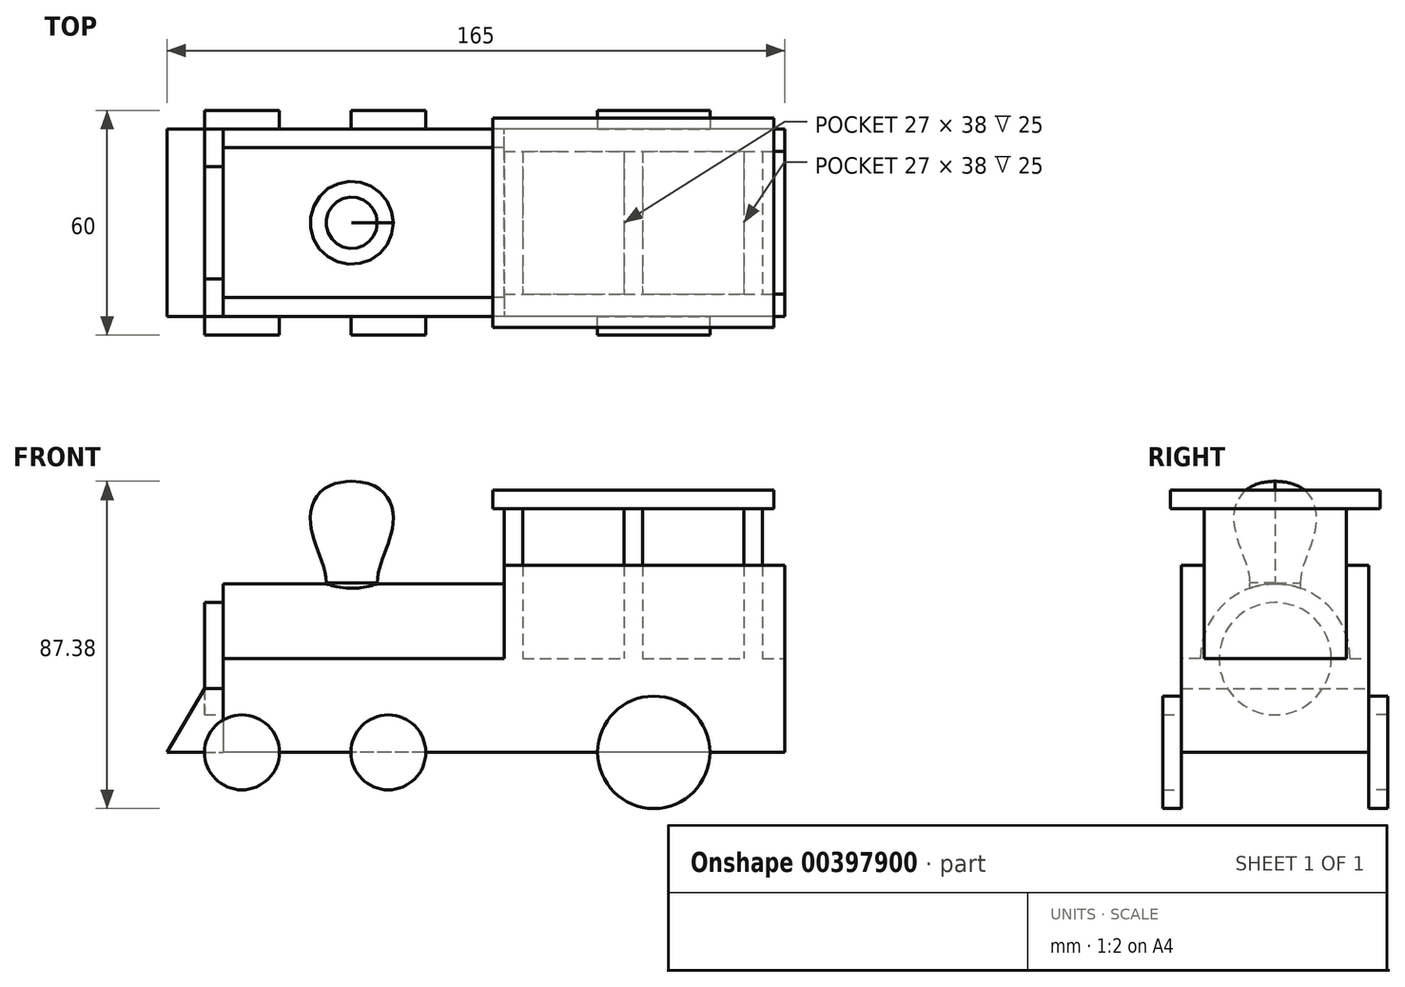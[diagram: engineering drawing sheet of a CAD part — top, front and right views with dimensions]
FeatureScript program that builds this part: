
annotation { "Feature Type Name" : "Feature", "Feature Type Description" : "" }
export const myFeature = defineFeature(function(context is Context, id is Id, definition is map)
    precondition{}
    {
        {
            var Q0;
            Q0=qCreatedBy(makeId("Top.planeOp"),FACE);
            var sketch = newSketch(context, id + "F0", { "sketchPlane" : qUnion([Q0])});
            skLineSegment(sketch, "E0.bottom", {"start": v(75, 25) * mm, "end": v(-75, 25) * mm});
            skLineSegment(sketch, "E0.top", {"start": v(75, -25) * mm, "end": v(-75, -25) * mm});
            skLineSegment(sketch, "E0.left", {"start": v(75, 25) * mm, "end": v(75, -25) * mm});
            skLineSegment(sketch, "E0.right", {"start": v(-75, 25) * mm, "end": v(-75, -25) * mm});
            skPoint(sketch, "E0.middle", {"position": v(0, 0) * mm});
            skSolve(sketch);
        }
        {
            var Q0;
            Q0=makeQuery(id+"F0.imprint","IMPRINT",FACE,{"disambiguationData":[TD([[makeQuery(id+"F0.imprint","IMPRINT",EDGE,{"derivedFrom":sQuery(id+"F0.wireOp",EDGE,"E0.bottom")}),1.0]])]});
            extrude(context, id + "F1", {"entities" : qUnion([Q0]), "depth" : 25 * mm});
        }
        {
            var Q0;
            Q0=makeQuery(id+"F1.opExtrude","SWEPT_FACE",FACE,{"disambiguationData":[OSD([sQuery(id+"F0.wireOp",EDGE,"E0.right")])]});
            var sketch = newSketch(context, id + "F2", { "sketchPlane" : qUnion([Q0])});
            skCircle(sketch, "E1", {"center": v(0, 25) * mm, "radius": 20 * mm});
            skSolve(sketch);
        }
        {
            var Q0;
            Q0=makeQuery(id+"F1.opExtrude","CAP_FACE",FACE,{"disambiguationData":[OSD([sQuery(id+"F0.wireOp",EDGE,"E0.bottom"),sQuery(id+"F0.wireOp",EDGE,"E0.top"),sQuery(id+"F0.wireOp",EDGE,"E0.left"),sQuery(id+"F0.wireOp",EDGE,"E0.right")])],"isStart":false});
            var sketch = newSketch(context, id + "F3", { "sketchPlane" : qUnion([Q0])});
            skLineSegment(sketch, "E2", {"start": v(0, 25) * mm, "end": v(0, -25) * mm, "construction": true});
            skSolve(sketch);
        }
        {
            var Q0;
            {var subQ0=sQuery(id+"F2.wireOp",EDGE,"E1");var subQ1=makeQuery(id+"F1.opExtrude","CAP_EDGE",EDGE,{"disambiguationData":[OSD([sQuery(id+"F0.wireOp",EDGE,"E0.right")])],"isStart":false});var subQ2=makeQuery(id+"F2.imprint","INTERSECT",VERTEX,{"disambiguationData":[OD(0.0)],"derivedFrom":[subQ1,subQ0]});Q0=makeQuery(id+"F2.imprint","IMPRINT",FACE,{"disambiguationData":[TD([[makeQuery(id+"F2.imprint","IMPRINT",EDGE,{"disambiguationData":[TD([[subQ2,1.0]])],"derivedFrom":subQ0}),1.0]])]});}
            extrude(context, id + "F4", {"entities" : qUnion([Q0]), "operationType" : NewBodyOperationType.ADD, "oppositeDirection" : true, "depth" : 75 * mm});
        }
        {
            var Q0;
            Q0=makeQuery(id+"F3.imprint","IMPRINT",FACE,{"disambiguationData":[TD([[makeQuery(id+"F3.imprint","IMPRINT",EDGE,{"derivedFrom":makeQuery(id+"F1.opExtrude","CAP_EDGE",EDGE,{"disambiguationData":[OSD([sQuery(id+"F0.wireOp",EDGE,"E0.bottom")])],"isStart":false})}),1.0]])]});
            var sketch = newSketch(context, id + "F5", { "sketchPlane" : qUnion([Q0])});
            skLineSegment(sketch, "E3.bottom", {"start": v(5, 19) * mm, "end": v(0, 19) * mm});
            skLineSegment(sketch, "E3.top", {"start": v(5, -19) * mm, "end": v(0, -19) * mm});
            skLineSegment(sketch, "E3.left", {"start": v(5, 19) * mm, "end": v(5, -19) * mm});
            skLineSegment(sketch, "E3.right", {"start": v(0, 19) * mm, "end": v(0, -19) * mm});
            skPoint(sketch, "E3.middle", {"position": v(2.5, 0) * mm});
            skLineSegment(sketch, "E4.1.0.0", {"start": v(32, 19) * mm, "end": v(32, -19) * mm});
            skLineSegment(sketch, "E4.1.0.1", {"start": v(37, -19) * mm, "end": v(32, -19) * mm});
            skLineSegment(sketch, "E4.1.0.2", {"start": v(37, 19) * mm, "end": v(37, -19) * mm});
            skLineSegment(sketch, "E4.1.0.3", {"start": v(37, 19) * mm, "end": v(32, 19) * mm});
            skPoint(sketch, "E4.1.0.4", {"position": v(34.5, 0) * mm});
            skLineSegment(sketch, "E4.2.0.0", {"start": v(64, 19) * mm, "end": v(64, -19) * mm});
            skLineSegment(sketch, "E4.2.0.1", {"start": v(69, -19) * mm, "end": v(64, -19) * mm});
            skLineSegment(sketch, "E4.2.0.2", {"start": v(69, 19) * mm, "end": v(69, -19) * mm});
            skLineSegment(sketch, "E4.2.0.3", {"start": v(69, 19) * mm, "end": v(64, 19) * mm});
            skPoint(sketch, "E4.2.0.4", {"position": v(66.5, 0) * mm});
            skLineSegment(sketch, "E4.direction1", {"start": v(0, -19) * mm, "end": v(32, -19) * mm, "construction": true});
            skSolve(sketch);
        }
        {
            var Q0;
            Q0 = qSketchRegion(id + "F5", true);
            extrude(context, id + "F6", {"entities" : qUnion([Q0]), "operationType" : NewBodyOperationType.ADD, "depth" : 40 * mm});
        }
        {
            var Q0;
            Q0=makeQuery(id+"F3.imprint","IMPRINT",FACE,{"disambiguationData":[TD([[makeQuery(id+"F3.imprint","IMPRINT",EDGE,{"derivedFrom":makeQuery(id+"F1.opExtrude","CAP_EDGE",EDGE,{"disambiguationData":[OSD([sQuery(id+"F0.wireOp",EDGE,"E0.bottom")])],"isStart":false})}),1.0]])]});
            var sketch = newSketch(context, id + "F7", { "sketchPlane" : qUnion([Q0])});
            skLineSegment(sketch, "E5.bottom", {"start": v(0, 19) * mm, "end": v(75, 19) * mm});
            skLineSegment(sketch, "E5.top", {"start": v(0, 25) * mm, "end": v(75, 25) * mm});
            skLineSegment(sketch, "E5.left", {"start": v(0, 19) * mm, "end": v(0, 25) * mm});
            skLineSegment(sketch, "E5.right", {"start": v(75, 19) * mm, "end": v(75, 25) * mm});
            skPoint(sketch, "E5.middle", {"position": v(37.5, 22) * mm});
            skLineSegment(sketch, "E6.MirrorCS", {"start": v(0, -19) * mm, "end": v(0, -25) * mm});
            skLineSegment(sketch, "E7.MirrorCS", {"start": v(75, -19) * mm, "end": v(75, -25) * mm});
            skLineSegment(sketch, "E8.MirrorCS", {"start": v(0, -19) * mm, "end": v(75, -19) * mm});
            skLineSegment(sketch, "E9.MirrorCS", {"start": v(0, -25) * mm, "end": v(75, -25) * mm});
            skPoint(sketch, "E10.MirrorP", {"position": v(37.5, -22) * mm});
            skSolve(sketch);
        }
        {
            var Q0;
            Q0 = qSketchRegion(id + "F7", true);
            extrude(context, id + "F8", {"entities" : qUnion([Q0]), "operationType" : NewBodyOperationType.ADD, "depth" : 25 * mm});
        }
        {
            var Q0;
            Q0=makeQuery(id+"F6.opExtrude","CAP_FACE",FACE,{"disambiguationData":[OSD([sQuery(id+"F5.wireOp",EDGE,"E3.bottom"),sQuery(id+"F5.wireOp",EDGE,"E3.top"),sQuery(id+"F5.wireOp",EDGE,"E3.left"),sQuery(id+"F5.wireOp",EDGE,"E3.right")])],"isStart":false});
            var sketch = newSketch(context, id + "F9", { "sketchPlane" : qUnion([Q0])});
            skLineSegment(sketch, "E11.bottom", {"start": v(72, 28) * mm, "end": v(-3, 28) * mm});
            skLineSegment(sketch, "E11.top", {"start": v(72, -28) * mm, "end": v(-3, -28) * mm});
            skLineSegment(sketch, "E11.left", {"start": v(72, 28) * mm, "end": v(72, -28) * mm});
            skLineSegment(sketch, "E11.right", {"start": v(-3, 28) * mm, "end": v(-3, -28) * mm});
            skPoint(sketch, "E11.middle", {"position": v(34.5, 0) * mm});
            skSolve(sketch);
        }
        {
            var Q0;
            Q0 = qSketchRegion(id + "F9", true);
            extrude(context, id + "F10", {"entities" : qUnion([Q0]), "operationType" : NewBodyOperationType.ADD, "depth" : 5 * mm});
        }
        {
            var Q0;
            {var subQ0=sQuery(id+"F0.wireOp",EDGE,"E0.right");Q0=makeQuery(id+"F4.boolean.opBoolean","MERGE",FACE,{"derivedFrom":[makeQuery(id+"F1.opExtrude","SWEPT_FACE",FACE,{"disambiguationData":[OSD([subQ0])]}),makeQuery(id+"F4.opExtrude","CAP_FACE",FACE,{"disambiguationData":[OSD([subQ0,sQuery(id+"F2.wireOp",EDGE,"E1")])],"isStart":true})]});}
            var sketch = newSketch(context, id + "F11", { "sketchPlane" : qUnion([Q0])});
            skCircle(sketch, "E12", {"center": v(0, 25) * mm, "radius": 15 * mm});
            skSolve(sketch);
        }
        {
            var Q0;
            Q0 = qSketchRegion(id + "F11", true);
            extrude(context, id + "F12", {"entities" : qUnion([Q0]), "operationType" : NewBodyOperationType.ADD, "depth" : 5 * mm});
        }
        {
            var Q0;
            Q0=makeQuery(id+"F8.boolean.opBoolean","MERGE",FACE,{"derivedFrom":[makeQuery(id+"F1.opExtrude","SWEPT_FACE",FACE,{"disambiguationData":[OSD([sQuery(id+"F0.wireOp",EDGE,"E0.bottom")])]}),makeQuery(id+"F8.opExtrude","SWEPT_FACE",FACE,{"disambiguationData":[OSD([sQuery(id+"F7.wireOp",EDGE,"E5.top")])]})]});
            var sketch = newSketch(context, id + "F13", { "sketchPlane" : qUnion([Q0])});
            skLineSegment(sketch, "E13", {"start": v(75, 17) * mm, "end": v(80, 17) * mm});
            skLineSegment(sketch, "E14", {"start": v(80, 17) * mm, "end": v(90, 0) * mm});
            skLineSegment(sketch, "E15", {"start": v(90, 0) * mm, "end": v(75, 0) * mm});
            skLineSegment(sketch, "E16", {"start": v(75, 0) * mm, "end": v(75, 17) * mm});
            skSolve(sketch);
        }
        {
            var Q0;
            Q0=makeQuery(id+"F13.imprint","IMPRINT",FACE,{"disambiguationData":[TD([[makeQuery(id+"F13.imprint","IMPRINT",EDGE,{"derivedFrom":sQuery(id+"F13.wireOp",EDGE,"E13")}),-1.0]])]});
            var Q1;
            Q1=makeQuery(id+"F8.boolean.opBoolean","MERGE",FACE,{"derivedFrom":[makeQuery(id+"F1.opExtrude","SWEPT_FACE",FACE,{"disambiguationData":[OSD([sQuery(id+"F0.wireOp",EDGE,"E0.top")])]}),makeQuery(id+"F8.opExtrude","SWEPT_FACE",FACE,{"disambiguationData":[OSD([sQuery(id+"F7.wireOp",EDGE,"E9.MirrorCS")])]})]});
            extrude(context, id + "F14", {"entities" : qUnion([Q0]), "endBound" : BoundingType.UP_TO_SURFACE, "oppositeDirection" : true, "endBoundEntityFace" : qUnion([Q1]), "depth" : 25 * mm});
        }
        {
            var Q0;
            Q0=qCreatedBy(makeId("Front.planeOp"),FACE);
            var sketch = newSketch(context, id + "F15", { "sketchPlane" : qUnion([Q0])});
            skLineSegment(sketch, "E17", {"start": v(-74.68, 45.2) * mm, "end": v(0, 45.2) * mm, "construction": true});
            skSolve(sketch);
        }
        {
            var Q0;
            Q0=qCreatedBy(makeId("Front.planeOp"),FACE);
            var sketch = newSketch(context, id + "F16", { "sketchPlane" : qUnion([Q0])});
            skLineSegment(sketch, "E18", {"start": v(-40.67, 45.2) * mm, "end": v(-40.67, 72.38) * mm});
            skFitSpline(sketch, "E19", {"points": [v(-40.67, 72.38) * mm, v(-29.74, 60.28) * mm, v(-33.85, 45.2) * mm], "startDerivative": vector(57.65, -1.07) * mm, "endDerivative": vector(0, -31.01) * mm});
            skLineSegment(sketch, "E20", {"start": v(-40.67, 45.2) * mm, "end": v(-33.85, 45.2) * mm});
            skSolve(sketch);
        }
        {
            var Q0;
            Q0=makeQuery(id+"F16.imprint","IMPRINT",FACE,{"disambiguationData":[TD([[makeQuery(id+"F16.imprint","IMPRINT",EDGE,{"derivedFrom":sQuery(id+"F16.wireOp",EDGE,"E18")}),-1.0]])]});
            var Q1;
            Q1=sQuery(id+"F16.wireOp",EDGE,"E18");
            revolve(context, id + "F17", {"operationType" : NewBodyOperationType.ADD, "entities" : qUnion([Q0]), "axis" : qUnion([Q1]), "revolveType" : RevolveType.FULL});
        }
        {
            var Q0;
            Q0=makeQuery(id+"F17.opRevolve","SWEPT_FACE",FACE,{"disambiguationData":[OSD([sQuery(id+"F16.wireOp",EDGE,"E20")])]});
            var Q1;
            Q1=makeQuery(id+"F4.opExtrude","SWEPT_FACE",FACE,{"disambiguationData":[OSD([sQuery(id+"F2.wireOp",EDGE,"E1")])]});
            extrude(context, id + "F18", {"entities" : qUnion([Q0]), "operationType" : NewBodyOperationType.ADD, "endBound" : BoundingType.UP_TO_SURFACE, "endBoundEntityFace" : qUnion([Q1]), "depth" : 25 * mm});
        }
        {
            var Q0;
            {Q0=qUnion([makeQuery(id+"F8.boolean.opBoolean","MERGE",FACE,{"derivedFrom":[makeQuery(id+"F1.opExtrude","SWEPT_FACE",FACE,{"disambiguationData":[OSD([sQuery(id+"F0.wireOp",EDGE,"E0.top")])]}),makeQuery(id+"F8.opExtrude","SWEPT_FACE",FACE,{"disambiguationData":[OSD([sQuery(id+"F7.wireOp",EDGE,"E9.MirrorCS")])]})]}),makeQuery(id+"F14.opExtrude","CAP_FACE",FACE,{"disambiguationData":[OSD([sQuery(id+"F13.wireOp",EDGE,"E13"),sQuery(id+"F13.wireOp",EDGE,"E14"),sQuery(id+"F13.wireOp",EDGE,"E15"),sQuery(id+"F13.wireOp",EDGE,"E16")])],"isStart":false})]);}
            var sketch = newSketch(context, id + "F19", { "sketchPlane" : qUnion([Q0])});
            skCircle(sketch, "E21", {"center": v(-70, 0) * mm, "radius": 10 * mm});
            skCircle(sketch, "E22.1.0.0", {"center": v(-30.9, 0) * mm, "radius": 10 * mm});
            skLineSegment(sketch, "E22.direction1", {"start": v(-70, 0) * mm, "end": v(-30.9, 0) * mm, "construction": true});
            skCircle(sketch, "E23", {"center": v(40, 0) * mm, "radius": 15 * mm});
            skSolve(sketch);
        }
        {
            var Q0;
            Q0 = qSketchRegion(id + "F19", true);
            extrude(context, id + "F20", {"entities" : qUnion([Q0]), "depth" : 5 * mm});
        }
        {
            var Q0;
            Q0=makeQuery(id+"F20.opExtrude","SWEPT_BODY",BODY,{"disambiguationData":[OSD([sQuery(id+"F19.wireOp",EDGE,"E21")])]});
            var Q1;
            Q1=makeQuery(id+"F20.opExtrude","SWEPT_BODY",BODY,{"disambiguationData":[OSD([sQuery(id+"F19.wireOp",EDGE,"E22.1.0.0")])]});
            var Q2;
            Q2=makeQuery(id+"F20.opExtrude","SWEPT_BODY",BODY,{"disambiguationData":[OSD([sQuery(id+"F19.wireOp",EDGE,"E23")])]});
            var Q3;
            Q3=qCreatedBy(makeId("Front.planeOp"),FACE);
            mirror(context, id + "F21", {"entities" : qUnion([Q0, Q1, Q2]), "mirrorPlane" : qUnion([Q3])});
        }
    });
